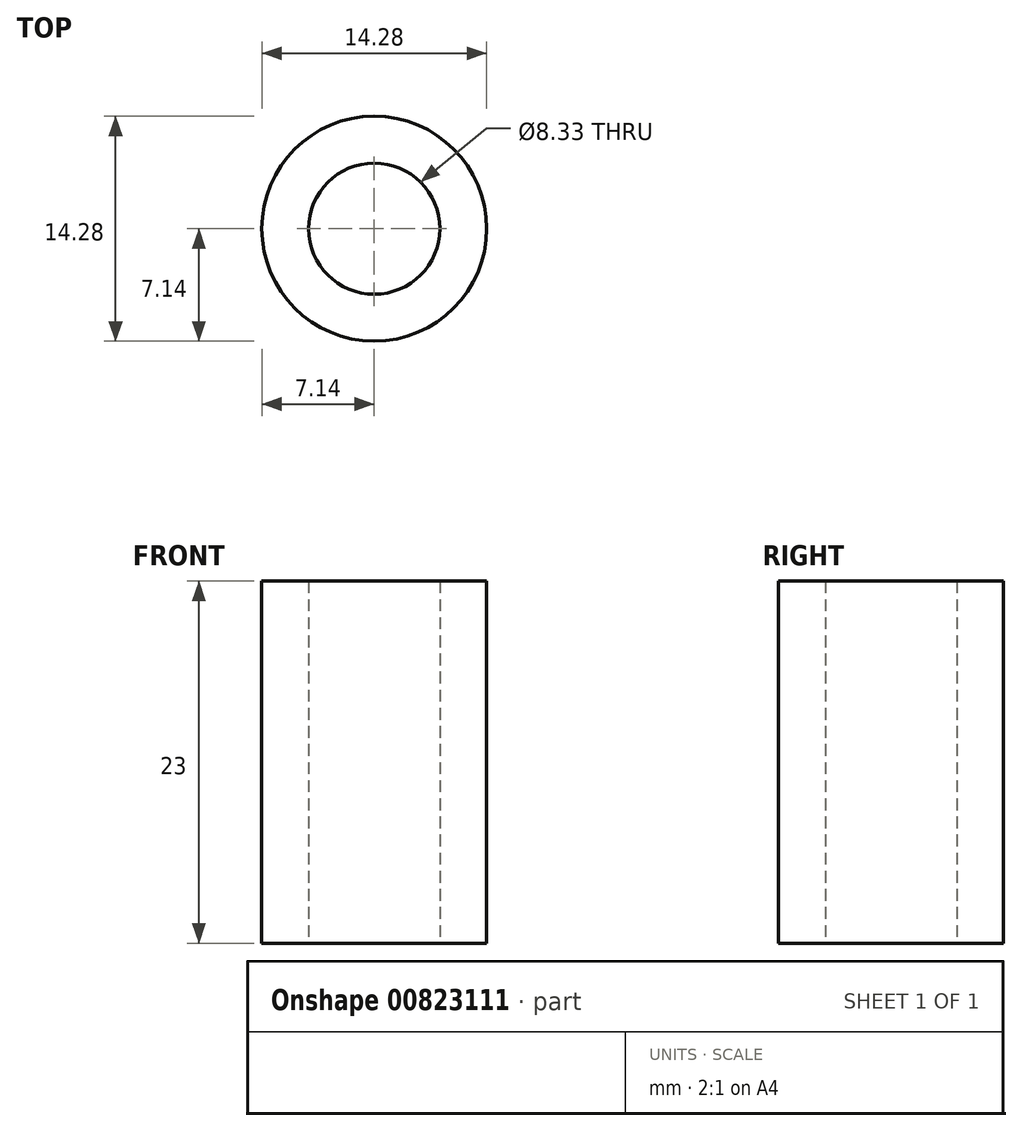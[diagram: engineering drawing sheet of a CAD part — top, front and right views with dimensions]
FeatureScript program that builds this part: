
annotation { "Feature Type Name" : "Feature", "Feature Type Description" : "" }
export const myFeature = defineFeature(function(context is Context, id is Id, definition is map)
    precondition{}
    {
        {
            var Q0;
            Q0=qCreatedBy(makeId("Top.planeOp"),FACE);
            var sketch = newSketch(context, id + "F0", { "sketchPlane" : qUnion([Q0])});
            skCircle(sketch, "E0", {"center": v(0, 0) * mm, "radius": 4.17 * mm});
            skCircle(sketch, "E1", {"center": v(0, 0) * mm, "radius": 7.14 * mm});
            skSolve(sketch);
        }
        {
            var Q0;
            Q0 = qSketchRegion(id + "F0", true);
            extrude(context, id + "F1", {"entities" : qUnion([Q0]), "depth" : 23 * mm, "offsetDistance" : 25 * mm});
        }
    });
